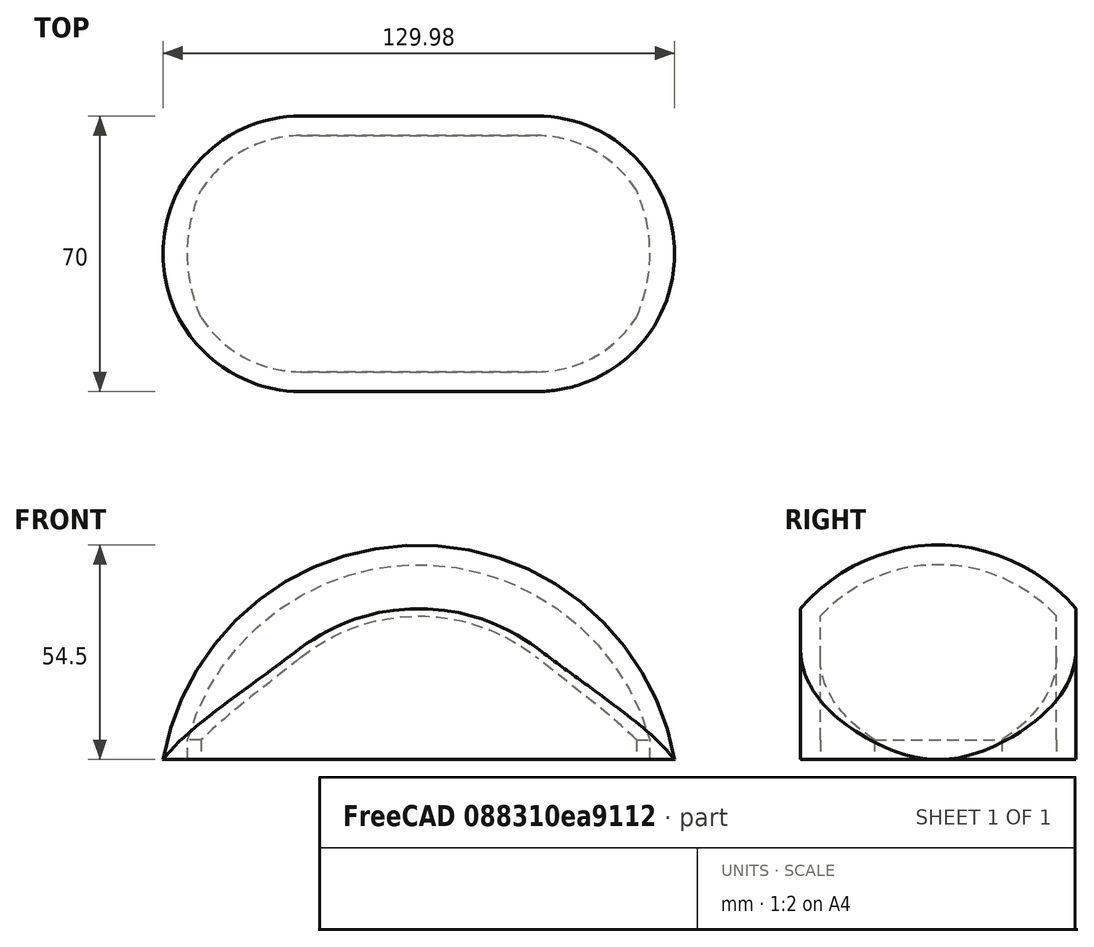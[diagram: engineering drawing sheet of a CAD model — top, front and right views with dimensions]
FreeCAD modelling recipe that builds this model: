
FCSTD DOCUMENT  (FreeCAD 0.16RUnknown)
Label: Art1BodyP3B
License: CreativeCommons Attribution-ShareAlike
LicenseURL: http://creativecommons.org/licenses/by-sa/4.0/
objects: Sketcher::SketchObject×2, Part::Cut×2, Part::Feature×2, Mesh::Feature×1, PartDesign::Pad×1, PartDesign::Revolution×1, Part::FeaturePython×1, Part::Offset×1, Part::Extrusion×1, Part::MultiFuse×1
note: 14 computed .brp shape members not serialized (recipe doc carries the construction recipe); baked Part::Feature solids carry a one-line shape summary decoded from their .brp

FEATURE [Mesh::Feature] Art1Body_P3B
  Placement = pos=(0,0,77) rot=(-1,0,0;1.5708rad)
FEATURE [Sketcher::SketchObject] Sketch
  Placement = pos=(0,0,77) rot=(0,0,1;0rad)
  sketch-geometry (4):
    g0: ArcOfCircle CenterX=-30 CenterY=0 CenterZ=0 NormalX=0 NormalY=0 NormalZ=1 Radius=35 StartAngle=1.5708 EndAngle=4.71239
    g1: ArcOfCircle CenterX=30 CenterY=0 CenterZ=0 NormalX=0 NormalY=0 NormalZ=1 Radius=35 StartAngle=4.71239 EndAngle=7.85398
    g2: LineSegment StartX=-30 StartY=-35 StartZ=0 EndX=30 EndY=-35 EndZ=0
    g3: LineSegment StartX=-30 StartY=35 StartZ=0 EndX=30 EndY=35 EndZ=0
  constraints (10):
    c: Tangent(g0,g3) = 1.5708
    c: Tangent(g0,g2) = -1.5708
    c: Tangent(g2,g1) = -1.5708
    c: Tangent(g3,g1) = 1.5708
    c: Horizontal(g2)
    c: Equal(g0,g1)
    c: PointOnObject(g0,g-1)
    c: DistanceX(g1) = 30
    c: Radius(g1) = 35
    c: Symmetric(g0,g1,g-2)
FEATURE [PartDesign::Pad] Pad
  Length = 55
  Length2 = 100
  Placement = pos=(0,0,77) rot=(0,0,1;0rad)
  Sketch = -> Sketch
  Type = 0
FEATURE [Sketcher::SketchObject] Sketch001
  Placement = pos=(0,0,65.5) rot=(0,0,1;0rad)
  sketch-geometry (6):
    g0: LineSegment StartX=20 StartY=46 StartZ=0 EndX=20 EndY=51 EndZ=0
    g1: LineSegment StartX=20 StartY=51 StartZ=0 EndX=120 EndY=51 EndZ=0
    g2: LineSegment StartX=120 StartY=51 StartZ=0 EndX=120 EndY=-51 EndZ=0
    g3: LineSegment StartX=120 StartY=-51 StartZ=0 EndX=20 EndY=-51 EndZ=0
    g4: LineSegment StartX=20 StartY=-51 StartZ=0 EndX=20 EndY=-46 EndZ=0
    g5: ArcOfCircle CenterX=20 CenterY=0 CenterZ=0 NormalX=0 NormalY=0 NormalZ=1 Radius=46 StartAngle=4.71239 EndAngle=7.85398
  constraints (19):
    c: Vertical(g0)
    c: Coincident(g0,g1)
    c: Horizontal(g1)
    c: Coincident(g1,g2)
    c: Vertical(g2)
    c: Coincident(g2,g3)
    c: Horizontal(g3)
    c: Coincident(g3,g4)
    c: Vertical(g4)
    c: PointOnObject(g5,g-1)
    c: Coincident(g5,g4)
    c: Coincident(g5,g0)
    c: Distance(g1) = 100
    c: DistanceX(g5) = 20
    c: Radius(g5) = 46
    c: Symmetric(g0,g4,g-1)
    c: Angle(g5) = 3.14159
    c: Equal(g0,g4)
    c: DistanceY(g0,g0) = 5
FEATURE [PartDesign::Revolution] Revolution
  Angle = 180
  Axis = (0,1,0)
  Base = (0,0,65.5)
  Placement = pos=(0,0,65.5) rot=(0,0,1;0rad)
  ReferenceAxis = -> Sketch001 [V_Axis]
  Reversed = true
  Sketch = -> Sketch001
FEATURE [Part::Cut] Cut  label="body"
  Base = -> Pad
  Tool = -> Revolution
FEATURE [Part::FeaturePython] Clone  label="Clone of body"  # Draft clone (typed FeaturePython)
  Objects = -> [Cut]
  Scale = (1,1,1)
FEATURE [Part::Offset] Offset  label="internalCavity"
  Fill = false
  Intersection = false
  Join = 0
  Mode = 0
  SelfIntersection = false
  Source = -> Clone
  Value = -5
FEATURE [Part::Feature] Face
  shape: bbox 117.5 x 60 x 0.002 mm, 1 faces, 0 solids (baked)
FEATURE [Part::Extrusion] Extrusion
  Base = -> Face
  Dir = (0,0,-5)
  Solid = true
FEATURE [Part::Feature] Offset_solid  label="internalCavity_(Solid)"
  shape: bbox 137.1 x 77.32 x 62.11 mm, 8 faces (baked)
FEATURE [Part::MultiFuse] Fusion  label="internalCavityTotal"
  Shapes = -> [Extrusion,Offset_solid]
FEATURE [Part::Cut] Cut001  label="bodyWithCavity"
  Base = -> Cut
  Tool = -> Fusion
